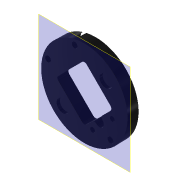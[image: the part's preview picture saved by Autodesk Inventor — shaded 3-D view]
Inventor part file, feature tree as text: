
AUTODESK INVENTOR PART (.ipt)
format: ipt  version: 2022 (Build 260153000, 153)  size: 240,640 bytes
history: native  units: in
note: dims shown in document units (in); Inventor stores cm internally (conversion verified against a paired STEP export)
features: reference x9, other x7, sketch x4, extrude x3, plane x1, hole x1, fillet x1, projected_geometry x1
ambient origin geometry x8: Origin, YZ Plane, XZ Plane, XY Plane, X Axis, Y Axis, Z Axis, Center Point
bodies: Solid1 (feature_tree)
feature tree (27):
  plane  "Work Plane1"
  extrude  "Extrusion1"  Depth=0.1575in
  hole  "Bohrung1"  [1 undecoded]
  fillet  "Rundung1"  Radius=0.9843in
  extrude  "Extrusion4"  Depth=0.0069in
  extrude  "Extrusion5"  Depth=0.0069in
  sketch  "Sketch1"  dims[d0=0.2756in d1=-0.0069in]
  reference  "Reference1"
  reference  "Reference5"
  reference  "Reference6"
  reference  "Reference7"
  sketch  "Skizze4"  dims[d9=0.1417in d10=0.75in d11=0.2559in d12=0.1575in d13=0.5635in d14=1.0in d15=0.8108in d17=0.9843in]
  reference  "Referenz9"
  reference  "Referenz10"
  reference  "Referenz11"
  reference  "Referenz12"
  reference  "Referenz13"
  sketch  "Skizze6"  dims[d18=0.9843in d19=45.0deg d20=0.9843in]
  projected_geometry  "Projizierte Kontur1"
  sketch  "Skizze7"  dims[d21=0.0787in d22=0.0787in d23=0.1102in d24=0.1102in d25=0.1575in d26=0.1575in d27=0.1575in d28=0.0014in d29=0.0069in d30=0.0787in d31=0.0in d32=2.126in]
  other  "<userpath>\Documents\Matchboxscope\INVENTOR\Matchboxscope_v1.iam"
  other  "Matchboxscope_v1.iam"
  other  "Matchboxscope_middle2_v1:1"
  other  "Matchboxscope_VCM_v1.iam"
  other  "Matchboxscope_middle2_m12VCMLens_v2:1"
  other  "Assembly_Matchboxscope_injectionmolded.iam"
  other  "IM_Matchboxscope_base:1"
note: 1 required parameter value undecoded (feature->parameter linkage not recoverable at this tier; creation-order binding heuristic only, values carry confidence <= 0.55)
